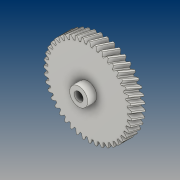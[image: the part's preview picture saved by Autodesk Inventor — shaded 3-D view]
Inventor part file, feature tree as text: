
AUTODESK INVENTOR PART (.ipt)
format: ipt  version: 2021 (Build 250183000, 183)  size: 664,064 bytes
history: native  units: mm (DEFAULTED — no unit token found)
features: extrude x3, plane x3, other x3, sketch x3
ambient origin geometry x8: Origin, YZ Plane, XZ Plane, XY Plane, X Axis, Y Axis, Z Axis, Center Point
bodies: Solid1 (feature_tree)
feature tree (12):
  extrude  "Extrusion1"  Depth=15.0mm TaperAngle=0.0deg
  plane  "Work Plane2"
  plane  "Work Plane8"
  plane  "Work Plane9"
  other  "Spur Gear"
  sketch  "Sketch3"  dims[d16=70.0mm d17=0.0mm d34=0.730603mm d39=0.0mm d41=0.0mm d43=70.0mm d46=70.0mm d47=0.0mm d48=0.0mm d49=10.0mm d50=5.0mm d51=17.0mm d52=0.0mm d53=10.0mm d54=0.0mm]
  extrude  "Extrusion2"  Depth=10.0mm TaperAngle=0.0deg
  extrude  "Extrusion3"  Depth=10.0mm TaperAngle=0.0deg
  sketch  "Sketch1"  dims[d0=97.176178mm d1=15.0mm d2=0.0mm]
  sketch  "Sketch2"  dims[d3=91.519288mm d4=10.0mm d5=0.0mm]
  other  "Srf1"
  other  "Pitch Diameter"
